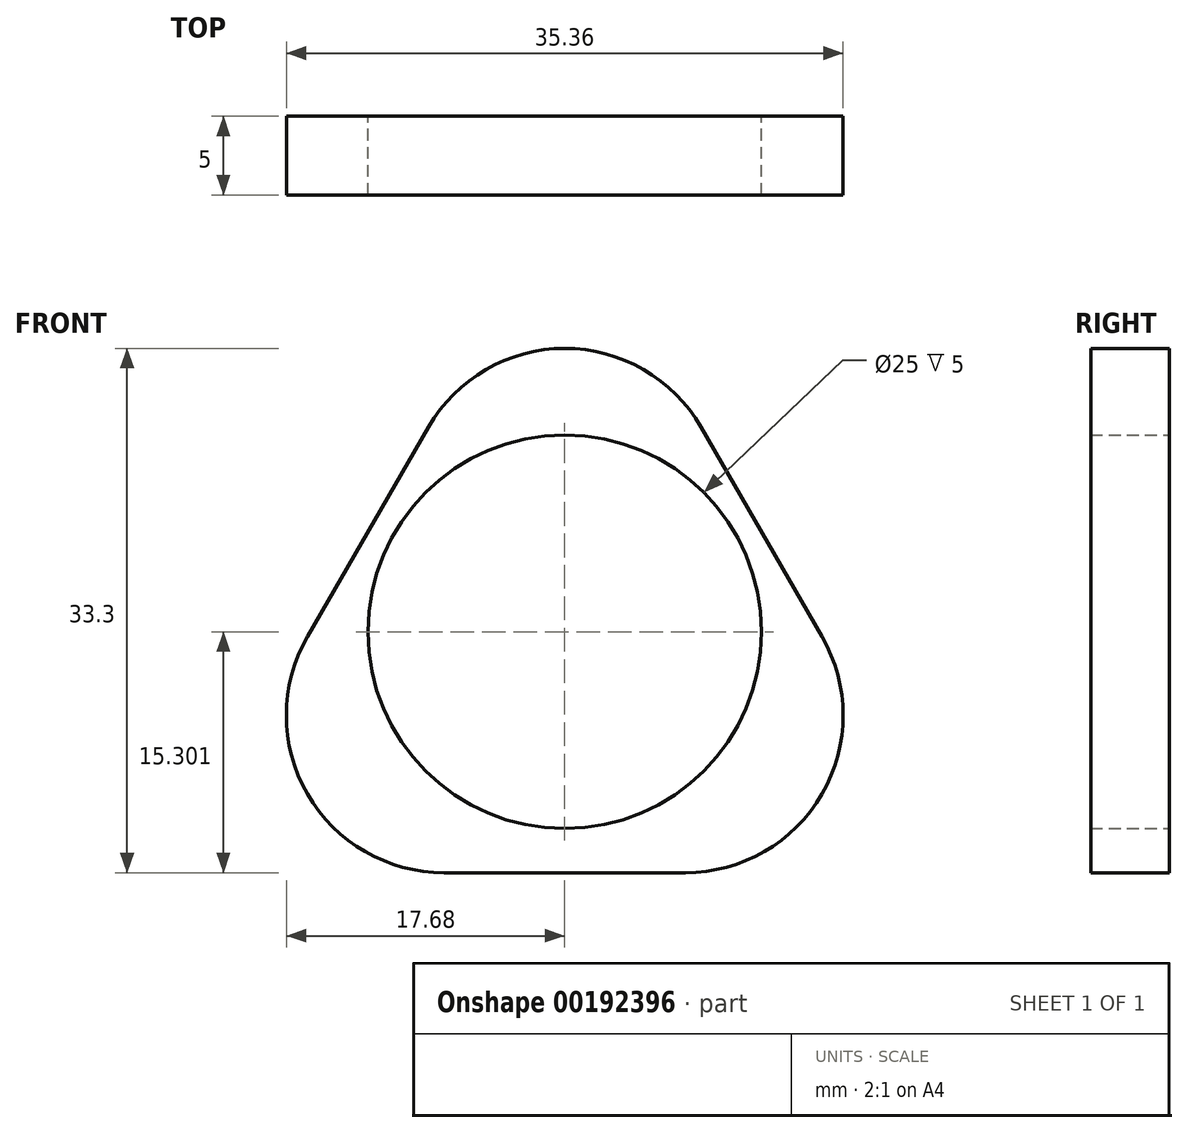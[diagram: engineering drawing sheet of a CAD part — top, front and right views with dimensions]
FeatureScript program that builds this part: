
annotation { "Feature Type Name" : "Feature", "Feature Type Description" : "" }
export const myFeature = defineFeature(function(context is Context, id is Id, definition is map)
    precondition{}
    {
        {
            var Q0;
            Q0=qCreatedBy(makeId("Front.planeOp"),FACE);
            var sketch = newSketch(context, id + "F0", { "sketchPlane" : qUnion([Q0])});
            skLineSegment(sketch, "E0", {"start": v(0, 0) * mm, "end": v(50, 0) * mm});
            skLineSegment(sketch, "E1", {"start": v(50, 0) * mm, "end": v(25, 43.3) * mm});
            skLineSegment(sketch, "E2", {"start": v(25, 43.3) * mm, "end": v(0, 0) * mm});
            skCircle(sketch, "E3", {"center": v(25, 15.3) * mm, "radius": 12.5 * mm});
            skSolve(sketch);
        }
        {
            var Q0;
            Q0 = qSketchRegion(id + "F0", true);
            extrude(context, id + "F1", {"entities" : qUnion([Q0]), "depth" : 5 * mm});
        }
        {
            var Q0;
            Q0=makeQuery(id+"F1.opExtrude","SWEPT_EDGE",EDGE,{"disambiguationData":[OSD([sQuery(id+"F0.wireOp",EDGE,"E1"),sQuery(id+"F0.wireOp",EDGE,"E2")])]});
            var Q1;
            Q1=makeQuery(id+"F1.opExtrude","SWEPT_EDGE",EDGE,{"disambiguationData":[OSD([sQuery(id+"F0.wireOp",EDGE,"E0"),sQuery(id+"F0.wireOp",EDGE,"E2")])]});
            var Q2;
            Q2=makeQuery(id+"F1.opExtrude","SWEPT_EDGE",EDGE,{"disambiguationData":[OSD([sQuery(id+"F0.wireOp",EDGE,"E0"),sQuery(id+"F0.wireOp",EDGE,"E1")])]});
            fillet(context, id + "F2", {"entities" : qUnion([Q0, Q1, Q2]), "radius" : 10 * mm, "tangentPropagation" : true, "allowEdgeOverflow" : false});
        }
    });
